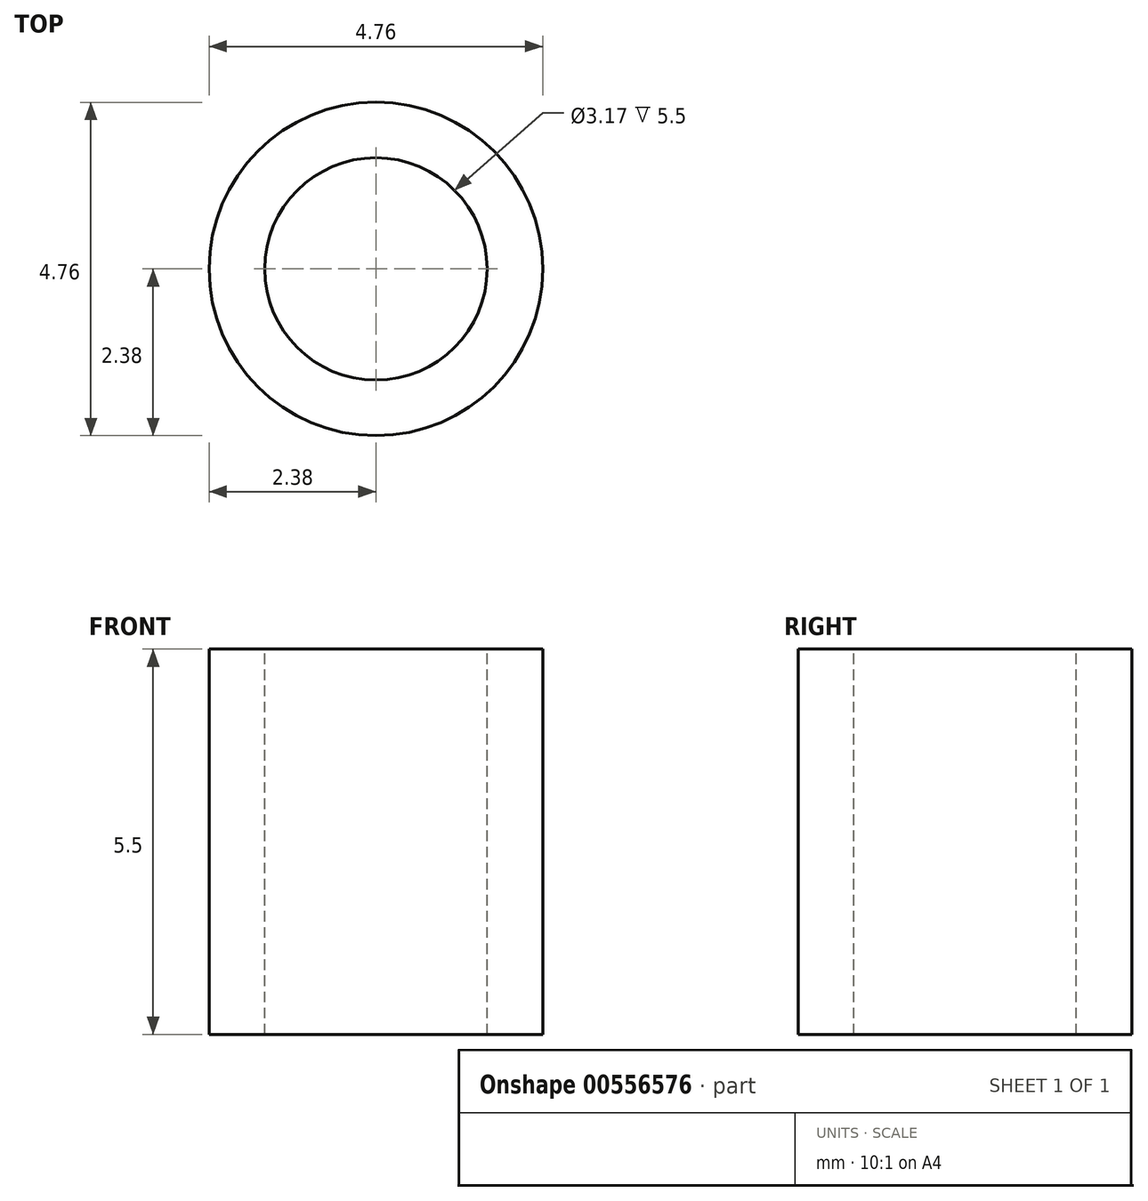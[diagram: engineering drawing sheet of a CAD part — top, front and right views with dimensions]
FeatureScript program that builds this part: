
annotation { "Feature Type Name" : "Feature", "Feature Type Description" : "" }
export const myFeature = defineFeature(function(context is Context, id is Id, definition is map)
    precondition{}
    {
        {
            var Q0;
            Q0=qCreatedBy(makeId("Top.planeOp"),FACE);
            var sketch = newSketch(context, id + "F0", { "sketchPlane" : qUnion([Q0])});
            skCircle(sketch, "E0", {"center": v(0, 0) * mm, "radius": 2.38 * mm});
            skSolve(sketch);
        }
        {
            var Q0;
            Q0 = qSketchRegion(id + "F0", true);
            extrude(context, id + "F1", {"entities" : qUnion([Q0]), "depth" : 5.5 * mm, "offsetDistance" : 25 * mm});
        }
        {
            var Q0;
            Q0=sQuery(id+"F0.wireOp",VERTEX,"E0.center");
            var Q1;
            Q1=makeQuery(id+"F1.opExtrude","SWEPT_BODY",BODY,{"disambiguationData":[OSD([sQuery(id+"F0.wireOp",EDGE,"E0")])]});
            hole(context, id + "F2", {"style" : HoleStyle.SIMPLE, "endStyle" : HoleEndStyle.THROUGH, "oppositeDirection" : true, "holeDiameter" : 3.17 * mm, "isTappedThrough" : true, "tappedDepth" : 12 * mm, "tapClearance" : 3, "locations" : qUnion([Q0]), "scope" : qUnion([Q1]), "startStyle" : HoleStartStyle.PART});
        }
    });
